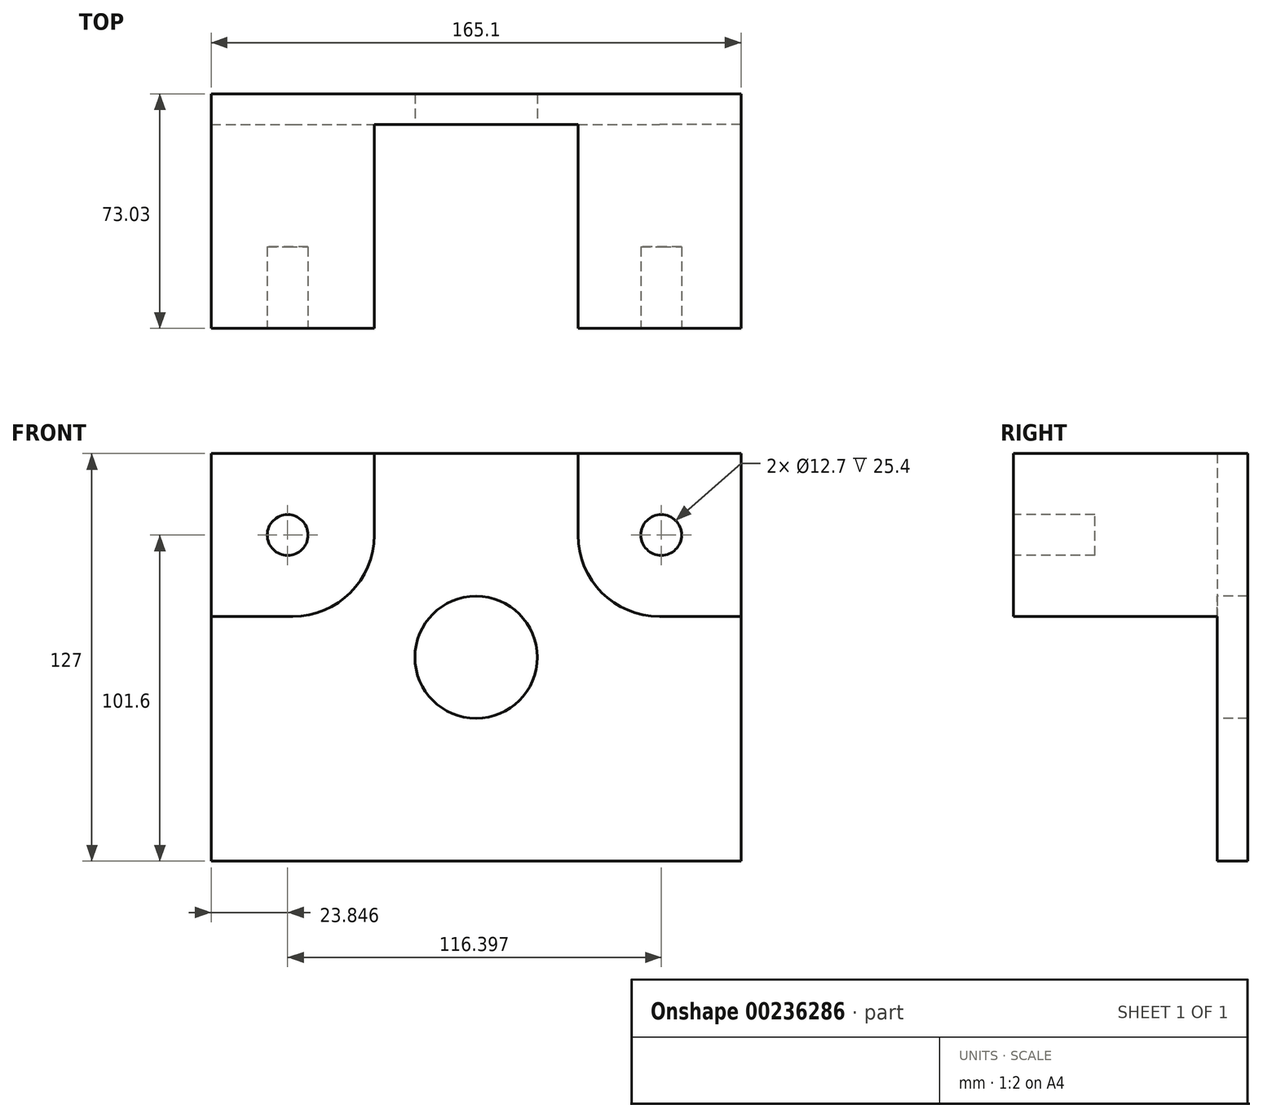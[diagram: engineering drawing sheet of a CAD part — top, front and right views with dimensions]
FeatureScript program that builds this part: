
annotation { "Feature Type Name" : "Feature", "Feature Type Description" : "" }
export const myFeature = defineFeature(function(context is Context, id is Id, definition is map)
    precondition{}
    {
        {
            var Q0;
            Q0=qCreatedBy(makeId("Front.planeOp"),FACE);
            var sketch = newSketch(context, id + "F0", { "sketchPlane" : qUnion([Q0])});
            skLineSegment(sketch, "E0.bottom", {"start": v(82.55, -63.5) * mm, "end": v(-82.55, -63.5) * mm});
            skLineSegment(sketch, "E0.top", {"start": v(82.55, 63.5) * mm, "end": v(-82.55, 63.5) * mm});
            skLineSegment(sketch, "E0.left", {"start": v(82.55, -63.5) * mm, "end": v(82.55, 63.5) * mm});
            skLineSegment(sketch, "E0.right", {"start": v(-82.55, -63.5) * mm, "end": v(-82.55, 63.5) * mm});
            skPoint(sketch, "E0.middle", {"position": v(0, 0) * mm});
            skSolve(sketch);
        }
        {
            var Q0;
            Q0 = qSketchRegion(id + "F0", true);
            var Q1;
            Q1=makeQuery(id+"F0.imprint","IMPRINT",FACE,{"disambiguationData":[TD([[makeQuery(id+"F0.imprint","IMPRINT",EDGE,{"derivedFrom":sQuery(id+"F0.wireOp",EDGE,"E0.bottom")}),-1.0]])]});
            extrude(context, id + "F1", {"entities" : qUnion([Q0, Q1]), "depth" : 9.52 * mm});
        }
        {
            var Q0;
            Q0=makeQuery(id+"F1.opExtrude","CAP_FACE",FACE,{"disambiguationData":[OSD([sQuery(id+"F0.wireOp",EDGE,"E0.bottom"),sQuery(id+"F0.wireOp",EDGE,"E0.top"),sQuery(id+"F0.wireOp",EDGE,"E0.left"),sQuery(id+"F0.wireOp",EDGE,"E0.right")])],"isStart":false});
            var sketch = newSketch(context, id + "F2", { "sketchPlane" : qUnion([Q0])});
            skLineSegment(sketch, "E1.bottom", {"start": v(-82.55, 63.5) * mm, "end": v(-31.75, 63.5) * mm});
            skLineSegment(sketch, "E1.top", {"start": v(-82.55, 12.7) * mm, "end": v(-57.15, 12.7) * mm});
            skLineSegment(sketch, "E1.left", {"start": v(-82.55, 63.5) * mm, "end": v(-82.55, 12.7) * mm});
            skLineSegment(sketch, "E1.right", {"start": v(-31.75, 63.5) * mm, "end": v(-31.75, 38.1) * mm});
            skLineSegment(sketch, "E2.bottom", {"start": v(82.55, 63.5) * mm, "end": v(31.75, 63.5) * mm});
            skLineSegment(sketch, "E2.top", {"start": v(82.55, 12.7) * mm, "end": v(57.15, 12.7) * mm});
            skLineSegment(sketch, "E2.left", {"start": v(82.55, 63.5) * mm, "end": v(82.55, 12.7) * mm});
            skLineSegment(sketch, "E2.right", {"start": v(31.75, 63.5) * mm, "end": v(31.75, 38.1) * mm});
            skPoint(sketch, "E3.visualSharp", {"position": v(-31.75, 12.7) * mm});
            skArc(sketch, "E3.filletArc", {"start": v(-57.15, 12.7) * mm, "mid": v(-39.19, 20.14) * mm, "end": v(-31.75, 38.1) * mm});
            skPoint(sketch, "E4.visualSharp", {"position": v(31.75, 12.7) * mm});
            skArc(sketch, "E4.filletArc", {"start": v(31.75, 38.1) * mm, "mid": v(39.19, 20.14) * mm, "end": v(57.15, 12.7) * mm});
            skSolve(sketch);
        }
        {
            var Q0;
            Q0=makeQuery(id+"F2.imprint","IMPRINT",FACE,{"disambiguationData":[TD([[makeQuery(id+"F2.imprint","IMPRINT",EDGE,{"derivedFrom":sQuery(id+"F2.wireOp",EDGE,"E2.bottom")}),1.0]])]});
            var Q1;
            Q1=makeQuery(id+"F2.imprint","IMPRINT",FACE,{"disambiguationData":[TD([[makeQuery(id+"F2.imprint","IMPRINT",EDGE,{"derivedFrom":sQuery(id+"F2.wireOp",EDGE,"E1.bottom")}),1.0]])]});
            extrude(context, id + "F3", {"entities" : qUnion([Q0, Q1]), "operationType" : NewBodyOperationType.ADD, "depth" : 63.5 * mm});
        }
        {
            var Q0;
            Q0=makeQuery(id+"F1.opExtrude","CAP_FACE",FACE,{"disambiguationData":[OSD([sQuery(id+"F0.wireOp",EDGE,"E0.bottom"),sQuery(id+"F0.wireOp",EDGE,"E0.top"),sQuery(id+"F0.wireOp",EDGE,"E0.left"),sQuery(id+"F0.wireOp",EDGE,"E0.right")])],"isStart":false});
            var sketch = newSketch(context, id + "F4", { "sketchPlane" : qUnion([Q0])});
            skCircle(sketch, "E5", {"center": v(0, 0) * mm, "radius": 19.05 * mm});
            skSolve(sketch);
        }
        {
            var Q0;
            Q0=makeQuery(id+"F3.opExtrude","CAP_FACE",FACE,{"disambiguationData":[OSD([sQuery(id+"F2.wireOp",EDGE,"E1.bottom"),sQuery(id+"F2.wireOp",EDGE,"E1.top"),sQuery(id+"F2.wireOp",EDGE,"E1.left"),sQuery(id+"F2.wireOp",EDGE,"E1.right"),sQuery(id+"F2.wireOp",EDGE,"E3.filletArc")])],"isStart":false});
            var sketch = newSketch(context, id + "F5", { "sketchPlane" : qUnion([Q0])});
            skCircle(sketch, "E6", {"center": v(-58.7, 38.1) * mm, "radius": 6.35 * mm});
            skSolve(sketch);
        }
        {
            var Q0;
            Q0=makeQuery(id+"F4.imprint","IMPRINT",FACE,{"disambiguationData":[TD([[makeQuery(id+"F4.imprint","IMPRINT",EDGE,{"derivedFrom":sQuery(id+"F4.wireOp",EDGE,"E5")}),1.0]])]});
            extrude(context, id + "F6", {"entities" : qUnion([Q0]), "operationType" : NewBodyOperationType.REMOVE, "oppositeDirection" : true, "depth" : 50.8 * mm});
        }
        {
            var Q0;
            Q0=makeQuery(id+"F5.imprint","IMPRINT",FACE,{"disambiguationData":[TD([[makeQuery(id+"F5.imprint","IMPRINT",EDGE,{"derivedFrom":sQuery(id+"F5.wireOp",EDGE,"E6")}),1.0]])]});
            extrude(context, id + "F7", {"entities" : qUnion([Q0]), "operationType" : NewBodyOperationType.REMOVE, "oppositeDirection" : true, "depth" : 25.4 * mm});
        }
        {
            var Q0;
            Q0=makeQuery(id+"F3.opExtrude","CAP_FACE",FACE,{"disambiguationData":[OSD([sQuery(id+"F2.wireOp",EDGE,"E2.bottom"),sQuery(id+"F2.wireOp",EDGE,"E2.top"),sQuery(id+"F2.wireOp",EDGE,"E2.left"),sQuery(id+"F2.wireOp",EDGE,"E2.right"),sQuery(id+"F2.wireOp",EDGE,"E4.filletArc")])],"isStart":false});
            var sketch = newSketch(context, id + "F8", { "sketchPlane" : qUnion([Q0])});
            skCircle(sketch, "E7", {"center": v(57.7, 38.1) * mm, "radius": 6.35 * mm});
            skSolve(sketch);
        }
        {
            var Q0;
            Q0=makeQuery(id+"F8.imprint","IMPRINT",FACE,{"disambiguationData":[TD([[makeQuery(id+"F8.imprint","IMPRINT",EDGE,{"derivedFrom":sQuery(id+"F8.wireOp",EDGE,"E7")}),1.0]])]});
            extrude(context, id + "F9", {"entities" : qUnion([Q0]), "operationType" : NewBodyOperationType.REMOVE, "oppositeDirection" : true, "depth" : 25.4 * mm});
        }
    });
